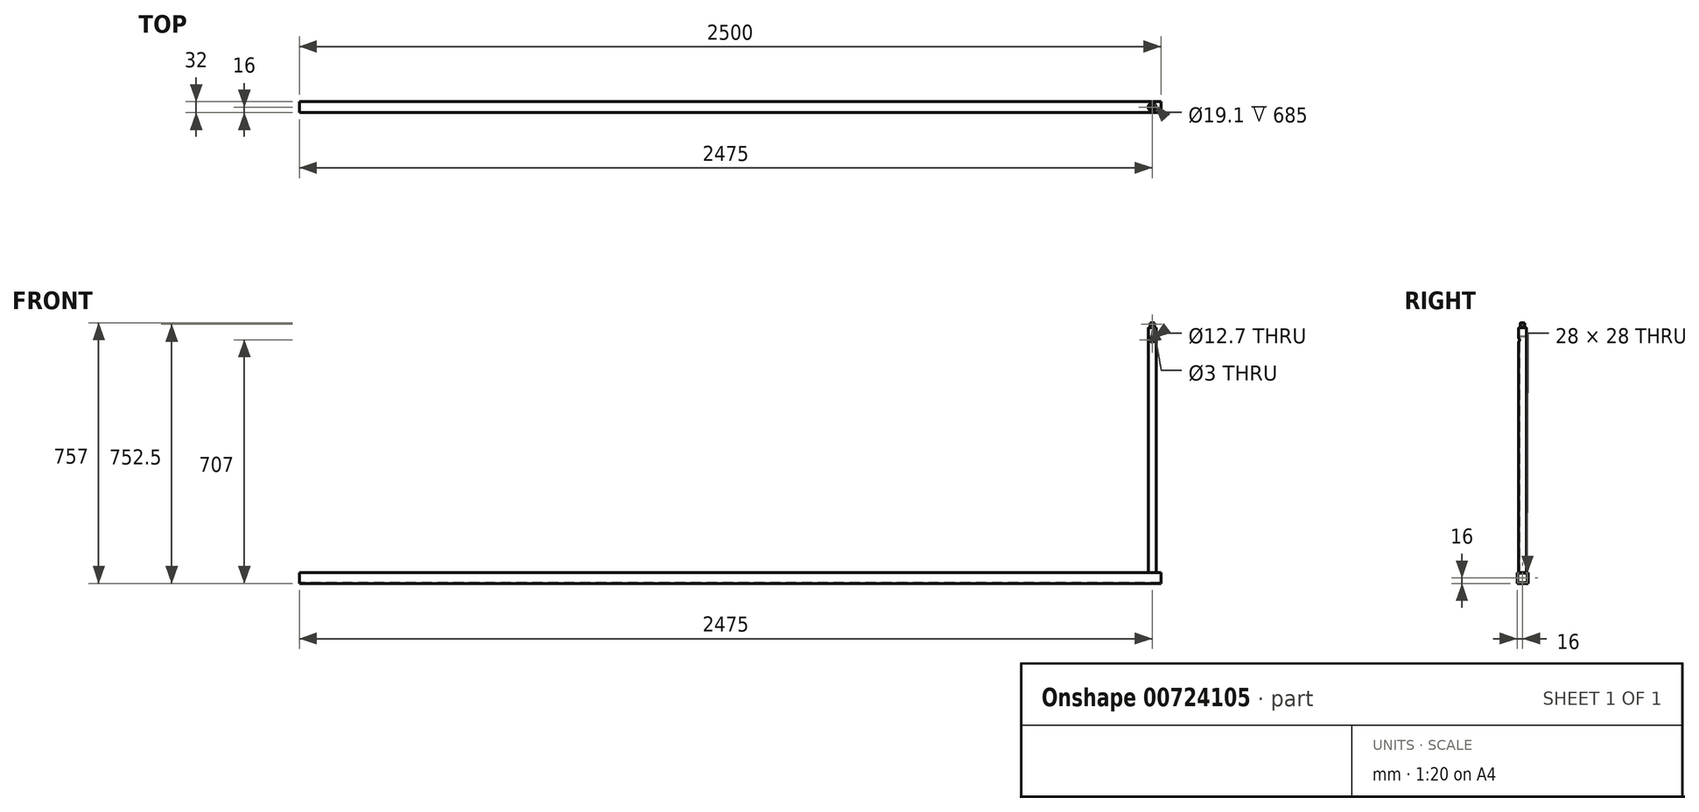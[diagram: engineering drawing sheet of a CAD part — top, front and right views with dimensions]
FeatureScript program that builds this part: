
annotation { "Feature Type Name" : "Feature", "Feature Type Description" : "" }
export const myFeature = defineFeature(function(context is Context, id is Id, definition is map)
    precondition{}
    {
        {
            var Q0;
            Q0=qCreatedBy(makeId("Right.planeOp"),FACE);
            var sketch = newSketch(context, id + "F0", { "sketchPlane" : qUnion([Q0])});
            skLineSegment(sketch, "E0.bottom", {"start": v(-16, 16) * mm, "end": v(16, 16) * mm});
            skLineSegment(sketch, "E0.top", {"start": v(-16, -16) * mm, "end": v(16, -16) * mm});
            skLineSegment(sketch, "E0.left", {"start": v(-16, 16) * mm, "end": v(-16, -16) * mm});
            skLineSegment(sketch, "E0.right", {"start": v(16, 16) * mm, "end": v(16, -16) * mm});
            skLineSegment(sketch, "E1.0", {"start": v(14, 14) * mm, "end": v(14, -14) * mm});
            skLineSegment(sketch, "E1.1", {"start": v(-14, 14) * mm, "end": v(14, 14) * mm});
            skLineSegment(sketch, "E1.2", {"start": v(-14, 14) * mm, "end": v(-14, -14) * mm});
            skLineSegment(sketch, "E1.3", {"start": v(-14, -14) * mm, "end": v(14, -14) * mm});
            skSolve(sketch);
        }
        {
            var Q0;
            Q0=qSketchRegion(id+"F0",true);
            extrude(context, id + "F1", {"entities" : qUnion([Q0]), "depth" : 25 * mm, "offsetDistance" : 25 * mm});
        }
        {
            var Q0;
            Q0=qSketchRegion(id+"F0",true);
            extrude(context, id + "F2", {"entities" : qUnion([Q0]), "operationType" : NewBodyOperationType.ADD, "oppositeDirection" : true, "depth" : 2475 * mm, "offsetDistance" : 25 * mm});
        }
        {
            var Q0;
            {var subQ0=sQuery(id+"F0.wireOp",EDGE,"E0.bottom");Q0=makeQuery(id+"F2.boolean.opBoolean","MERGE",FACE,{"derivedFrom":[makeQuery(id+"F1.opExtrude","SWEPT_FACE",FACE,{"disambiguationData":[OSD([subQ0])]}),makeQuery(id+"F2.opExtrude","SWEPT_FACE",FACE,{"disambiguationData":[OSD([subQ0])]})]});}
            var sketch = newSketch(context, id + "F3", { "sketchPlane" : qUnion([Q0])});
            skCircle(sketch, "E2", {"center": v(0, 0) * mm, "radius": 11.55 * mm});
            skCircle(sketch, "E3", {"center": v(0, 0) * mm, "radius": 9.55 * mm});
            skSolve(sketch);
        }
        {
            var Q0;
            Q0=qSketchRegion(id+"F3",true);
            extrude(context, id + "F4", {"entities" : qUnion([Q0]), "operationType" : NewBodyOperationType.ADD, "depth" : 710 * mm, "offsetDistance" : 25 * mm});
        }
        {
            var Q0;
            Q0=makeQuery(id+"F4.opExtrude","CAP_FACE",FACE,{"disambiguationData":[OSD([sQuery(id+"F3.wireOp",EDGE,"E2"),sQuery(id+"F3.wireOp",EDGE,"E3")])],"isStart":false});
            var sketch = newSketch(context, id + "F5", { "sketchPlane" : qUnion([Q0])});
            skCircle(sketch, "E4.0", {"center": v(0, 0) * mm, "radius": 9.55 * mm});
            skSolve(sketch);
        }
        {
            var Q0;
            Q0=qSketchRegion(id+"F5",true);
            extrude(context, id + "F6", {"entities" : qUnion([Q0]), "oppositeDirection" : true, "depth" : 25 * mm, "offsetDistance" : 25 * mm});
        }
        {
            var Q0;
            Q0=makeQuery(id+"F6.opExtrude","CAP_FACE",FACE,{"disambiguationData":[OSD([sQuery(id+"F5.wireOp",EDGE,"E4.0")])],"isStart":true});
            var sketch = newSketch(context, id + "F7", { "sketchPlane" : qUnion([Q0])});
            skCircle(sketch, "E5", {"center": v(0, 0) * mm, "radius": 6.35 * mm});
            skSolve(sketch);
        }
        {
            var Q0;
            Q0=qSketchRegion(id+"F7",true);
            extrude(context, id + "F8", {"entities" : qUnion([Q0]), "operationType" : NewBodyOperationType.ADD, "depth" : 15 * mm, "offsetDistance" : 25 * mm});
        }
        {
            var Q0;
            Q0=qCreatedBy(makeId("Front.planeOp"),FACE);
            var sketch = newSketch(context, id + "F9", { "sketchPlane" : qUnion([Q0])});
            skCircle(sketch, "E6", {"center": v(0, 736.5) * mm, "radius": 1.5 * mm});
            skSolve(sketch);
        }
        {
            var Q0;
            Q0=qSketchRegion(id+"F9",true);
            extrude(context, id + "F10", {"entities" : qUnion([Q0]), "operationType" : NewBodyOperationType.REMOVE, "endBound" : BoundingType.SYMMETRIC, "depth" : 13 * mm, "offsetDistance" : 25 * mm});
        }
        {
            var Q0;
            Q0=makeQuery(id+"F6.opExtrude","CAP_FACE",FACE,{"disambiguationData":[OSD([sQuery(id+"F5.wireOp",EDGE,"E4.0")])],"isStart":true});
            var sketch = newSketch(context, id + "F11", { "sketchPlane" : qUnion([Q0])});
            skCircle(sketch, "E7.0", {"center": v(0, 0) * mm, "radius": 6.35 * mm});
            skCircle(sketch, "E8.0", {"center": v(0, 0) * mm, "radius": 9.55 * mm});
            skSolve(sketch);
        }
        {
            var Q0;
            Q0=qSketchRegion(id+"F11",true);
            extrude(context, id + "F12", {"entities" : qUnion([Q0]), "operationType" : NewBodyOperationType.ADD, "depth" : 2 * mm, "offsetDistance" : 25 * mm});
        }
        {
            var Q0;
            Q0=qCreatedBy(makeId("Front.planeOp"),FACE);
            var sketch = newSketch(context, id + "F13", { "sketchPlane" : qUnion([Q0])});
            skLineSegment(sketch, "E9", {"start": v(0, 721.34) * mm, "end": v(0, 660.08) * mm, "construction": true});
            skCircle(sketch, "E10", {"center": v(0, 691) * mm, "radius": 6.35 * mm});
            skSolve(sketch);
        }
        {
            var Q0;
            Q0=qSketchRegion(id+"F13",true);
            extrude(context, id + "F14", {"entities" : qUnion([Q0]), "operationType" : NewBodyOperationType.REMOVE, "depth" : 25 * mm, "offsetDistance" : 25 * mm});
        }
    });
